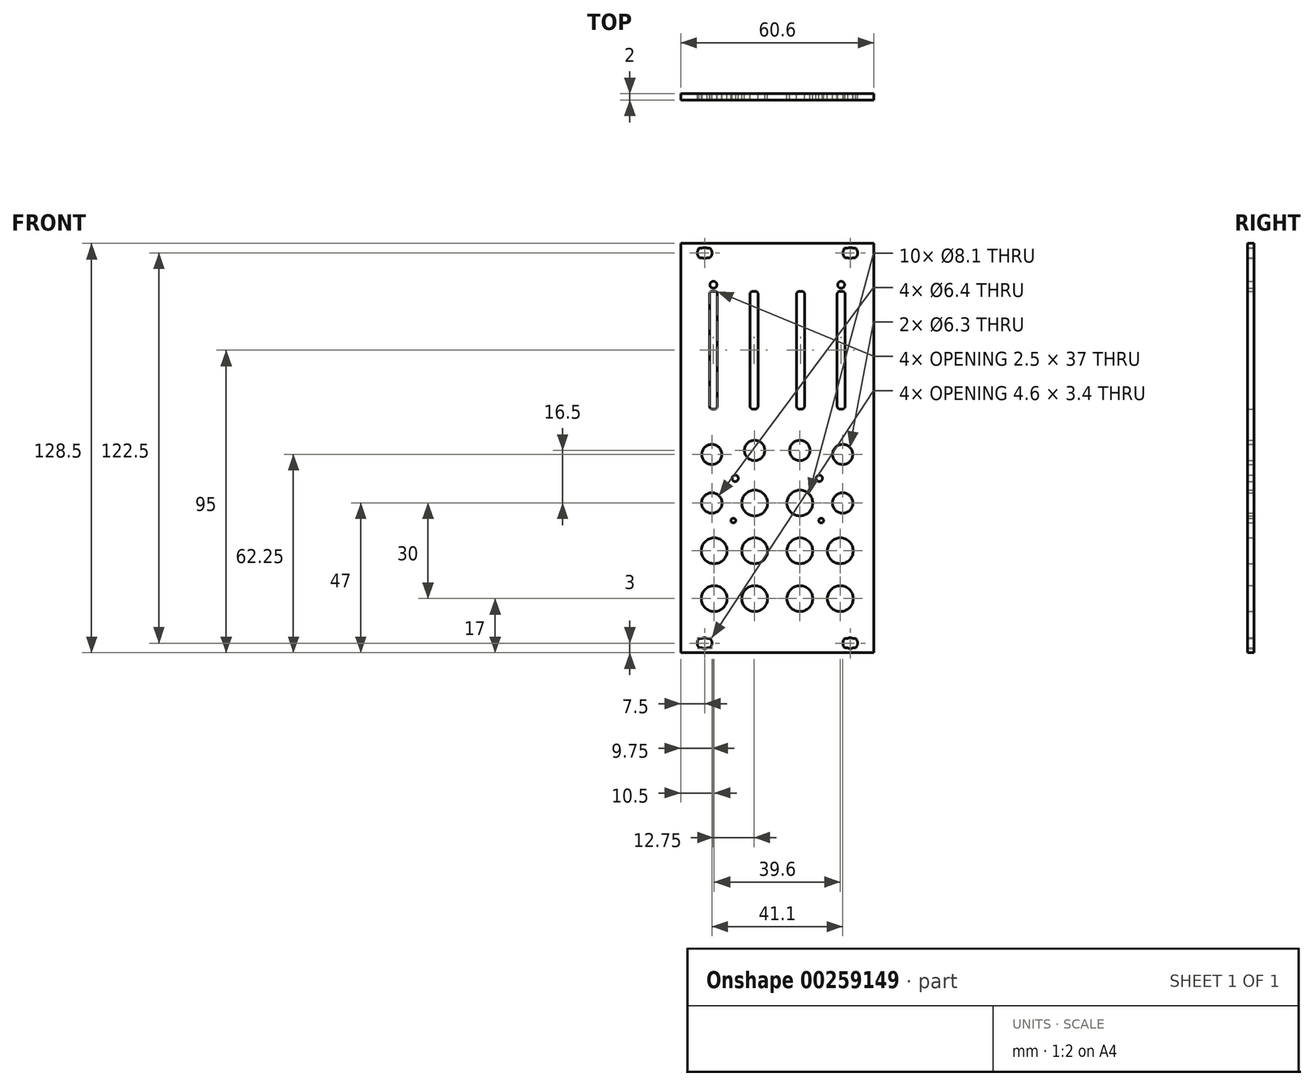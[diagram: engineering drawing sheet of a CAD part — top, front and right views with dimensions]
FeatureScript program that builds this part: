
annotation { "Feature Type Name" : "Feature", "Feature Type Description" : "" }
export const myFeature = defineFeature(function(context is Context, id is Id, definition is map)
    precondition{}
    {
        {
            var Q0;
            Q0=qCreatedBy(makeId("Front.planeOp"),FACE);
            var sketch = newSketch(context, id + "F0", { "sketchPlane" : qUnion([Q0])});
            skLineSegment(sketch, "E0", {"start": v(23.72, -59.75) * mm, "end": v(24.62, -59.75) * mm});
            skLineSegment(sketch, "E1", {"start": v(21.22, -59.75) * mm, "end": v(22.12, -59.75) * mm});
            skLineSegment(sketch, "E2", {"start": v(23.72, -62.75) * mm, "end": v(24.62, -62.75) * mm});
            skLineSegment(sketch, "E3", {"start": v(21.22, -62.75) * mm, "end": v(22.12, -62.75) * mm});
            skLineSegment(sketch, "E4", {"start": v(21.22, 59.75) * mm, "end": v(22.12, 59.75) * mm});
            skLineSegment(sketch, "E5", {"start": v(23.72, 59.75) * mm, "end": v(24.62, 59.75) * mm});
            skLineSegment(sketch, "E6", {"start": v(21.22, 62.75) * mm, "end": v(22.12, 62.75) * mm});
            skLineSegment(sketch, "E7", {"start": v(23.72, 62.75) * mm, "end": v(24.62, 62.75) * mm});
            skLineSegment(sketch, "E8", {"start": v(-30.3, -64.25) * mm, "end": v(-30.3, -61.25) * mm});
            skLineSegment(sketch, "E9", {"start": v(-30.3, 64.25) * mm, "end": v(30.3, 64.25) * mm});
            skLineSegment(sketch, "E10", {"start": v(30.3, -64.25) * mm, "end": v(30.3, 64.25) * mm});
            skLineSegment(sketch, "E11", {"start": v(-30.3, -64.25) * mm, "end": v(30.3, -64.25) * mm});
            skLineSegment(sketch, "E12", {"start": v(-30.3, -64.25) * mm, "end": v(-30.3, 64.25) * mm});
            skLineSegment(sketch, "E13", {"start": v(-22, -59.75) * mm, "end": v(-21.1, -59.75) * mm});
            skLineSegment(sketch, "E14", {"start": v(-24.5, -59.75) * mm, "end": v(-23.6, -59.75) * mm});
            skLineSegment(sketch, "E15", {"start": v(-22, -62.75) * mm, "end": v(-21.1, -62.75) * mm});
            skLineSegment(sketch, "E16", {"start": v(-24.5, -62.75) * mm, "end": v(-23.6, -62.75) * mm});
            skLineSegment(sketch, "E17", {"start": v(-22, 62.75) * mm, "end": v(-21.1, 62.75) * mm});
            skLineSegment(sketch, "E18", {"start": v(-24.5, 62.75) * mm, "end": v(-23.6, 62.75) * mm});
            skLineSegment(sketch, "E19", {"start": v(-22, 59.75) * mm, "end": v(-21.1, 59.75) * mm});
            skLineSegment(sketch, "E20", {"start": v(-24.5, 59.75) * mm, "end": v(-23.6, 59.75) * mm});
            skArc(sketch, "E21", {"start": v(21.22, -59.75) * mm, "mid": v(20.62, -61.25) * mm, "end": v(21.22, -62.75) * mm});
            skArc(sketch, "E22", {"start": v(24.62, -62.75) * mm, "mid": v(25.22, -61.25) * mm, "end": v(24.62, -59.75) * mm});
            skArc(sketch, "E23", {"start": v(23.72, -59.75) * mm, "mid": v(22.92, -59.55) * mm, "end": v(22.12, -59.75) * mm});
            skArc(sketch, "E24", {"start": v(22.12, -62.75) * mm, "mid": v(22.92, -62.95) * mm, "end": v(23.72, -62.75) * mm});
            skArc(sketch, "E25", {"start": v(22.12, 59.75) * mm, "mid": v(22.92, 59.55) * mm, "end": v(23.72, 59.75) * mm});
            skArc(sketch, "E26", {"start": v(23.72, 62.75) * mm, "mid": v(22.92, 62.95) * mm, "end": v(22.12, 62.75) * mm});
            skArc(sketch, "E27", {"start": v(24.62, 59.75) * mm, "mid": v(25.22, 61.25) * mm, "end": v(24.62, 62.75) * mm});
            skArc(sketch, "E28", {"start": v(21.22, 62.75) * mm, "mid": v(20.62, 61.25) * mm, "end": v(21.22, 59.75) * mm});
            skArc(sketch, "E29", {"start": v(-24.5, -59.75) * mm, "mid": v(-25.1, -61.25) * mm, "end": v(-24.5, -62.75) * mm});
            skArc(sketch, "E30", {"start": v(-21.1, -62.75) * mm, "mid": v(-20.5, -61.25) * mm, "end": v(-21.1, -59.75) * mm});
            skArc(sketch, "E31", {"start": v(-22, -59.75) * mm, "mid": v(-22.8, -59.55) * mm, "end": v(-23.6, -59.75) * mm});
            skArc(sketch, "E32", {"start": v(-23.6, -62.75) * mm, "mid": v(-22.8, -62.95) * mm, "end": v(-22, -62.75) * mm});
            skArc(sketch, "E33", {"start": v(-24.5, 62.75) * mm, "mid": v(-25.1, 61.25) * mm, "end": v(-24.5, 59.75) * mm});
            skArc(sketch, "E34", {"start": v(-21.1, 59.75) * mm, "mid": v(-20.5, 61.25) * mm, "end": v(-21.1, 62.75) * mm});
            skArc(sketch, "E35", {"start": v(-22, 62.75) * mm, "mid": v(-22.8, 62.95) * mm, "end": v(-23.6, 62.75) * mm});
            skArc(sketch, "E36", {"start": v(-23.6, 59.75) * mm, "mid": v(-22.8, 59.55) * mm, "end": v(-22, 59.75) * mm});
            skLineSegment(sketch, "E37", {"start": v(13.3, -22.75) * mm, "end": v(14.3, -22.75) * mm});
            skLineSegment(sketch, "E38", {"start": v(13.8, -23.25) * mm, "end": v(13.8, -22.25) * mm});
            skLineSegment(sketch, "E39", {"start": v(-20.55, -2.5) * mm, "end": v(-20.55, -1.5) * mm});
            skLineSegment(sketch, "E40", {"start": v(-21.05, -2) * mm, "end": v(-20.05, -2) * mm});
            skCircle(sketch, "E41", {"center": v(-20.55, -2) * mm, "radius": 3.15 * mm});
            skLineSegment(sketch, "E42", {"start": v(20.55, -2.5) * mm, "end": v(20.55, -1.5) * mm});
            skLineSegment(sketch, "E43", {"start": v(20.05, -2) * mm, "end": v(21.05, -2) * mm});
            skCircle(sketch, "E44", {"center": v(20.55, -2) * mm, "radius": 3.15 * mm});
            skLineSegment(sketch, "E45", {"start": v(6.05, 30.75) * mm, "end": v(6.05, 48.35) * mm});
            skLineSegment(sketch, "E46", {"start": v(6.05, 13.15) * mm, "end": v(6.05, 30.75) * mm});
            skLineSegment(sketch, "E47", {"start": v(6.95, 12.25) * mm, "end": v(7.65, 12.25) * mm});
            skLineSegment(sketch, "E48", {"start": v(7.3, 30.25) * mm, "end": v(7.3, 31.25) * mm});
            skLineSegment(sketch, "E49", {"start": v(8.55, 13.15) * mm, "end": v(8.55, 30.75) * mm});
            skLineSegment(sketch, "E50", {"start": v(6.8, 30.75) * mm, "end": v(7.8, 30.75) * mm});
            skLineSegment(sketch, "E51", {"start": v(6.95, 49.25) * mm, "end": v(7.65, 49.25) * mm});
            skLineSegment(sketch, "E52", {"start": v(8.55, 30.75) * mm, "end": v(8.55, 48.35) * mm});
            skArc(sketch, "E53", {"start": v(6.05, 13.15) * mm, "mid": v(6.31, 12.51) * mm, "end": v(6.95, 12.25) * mm});
            skArc(sketch, "E54", {"start": v(6.95, 49.25) * mm, "mid": v(6.31, 48.99) * mm, "end": v(6.05, 48.35) * mm});
            skArc(sketch, "E55", {"start": v(7.65, 12.25) * mm, "mid": v(8.29, 12.51) * mm, "end": v(8.55, 13.15) * mm});
            skArc(sketch, "E56", {"start": v(8.55, 48.35) * mm, "mid": v(8.29, 48.99) * mm, "end": v(7.65, 49.25) * mm});
            skLineSegment(sketch, "E57", {"start": v(-8.55, 30.75) * mm, "end": v(-8.55, 48.35) * mm});
            skLineSegment(sketch, "E58", {"start": v(-8.55, 13.15) * mm, "end": v(-8.55, 30.75) * mm});
            skLineSegment(sketch, "E59", {"start": v(-7.65, 12.25) * mm, "end": v(-6.95, 12.25) * mm});
            skLineSegment(sketch, "E60", {"start": v(-7.3, 30.25) * mm, "end": v(-7.3, 31.25) * mm});
            skLineSegment(sketch, "E61", {"start": v(-6.05, 13.15) * mm, "end": v(-6.05, 30.75) * mm});
            skLineSegment(sketch, "E62", {"start": v(-7.8, 30.75) * mm, "end": v(-6.8, 30.75) * mm});
            skLineSegment(sketch, "E63", {"start": v(-7.65, 49.25) * mm, "end": v(-6.95, 49.25) * mm});
            skLineSegment(sketch, "E64", {"start": v(-6.05, 30.75) * mm, "end": v(-6.05, 48.35) * mm});
            skArc(sketch, "E65", {"start": v(-8.55, 13.15) * mm, "mid": v(-8.29, 12.51) * mm, "end": v(-7.65, 12.25) * mm});
            skArc(sketch, "E66", {"start": v(-7.65, 49.25) * mm, "mid": v(-8.29, 48.99) * mm, "end": v(-8.55, 48.35) * mm});
            skArc(sketch, "E67", {"start": v(-6.95, 12.25) * mm, "mid": v(-6.31, 12.51) * mm, "end": v(-6.05, 13.15) * mm});
            skArc(sketch, "E68", {"start": v(-6.05, 48.35) * mm, "mid": v(-6.31, 48.99) * mm, "end": v(-6.95, 49.25) * mm});
            skLineSegment(sketch, "E69", {"start": v(18.8, 30.75) * mm, "end": v(18.8, 48.35) * mm});
            skLineSegment(sketch, "E70", {"start": v(18.8, 13.15) * mm, "end": v(18.8, 30.75) * mm});
            skLineSegment(sketch, "E71", {"start": v(19.7, 12.25) * mm, "end": v(20.4, 12.25) * mm});
            skLineSegment(sketch, "E72", {"start": v(20.05, 30.25) * mm, "end": v(20.05, 31.25) * mm});
            skLineSegment(sketch, "E73", {"start": v(21.3, 13.15) * mm, "end": v(21.3, 30.75) * mm});
            skLineSegment(sketch, "E74", {"start": v(19.55, 30.75) * mm, "end": v(20.55, 30.75) * mm});
            skLineSegment(sketch, "E75", {"start": v(19.7, 49.25) * mm, "end": v(20.4, 49.25) * mm});
            skLineSegment(sketch, "E76", {"start": v(21.3, 30.75) * mm, "end": v(21.3, 48.35) * mm});
            skArc(sketch, "E77", {"start": v(18.8, 13.15) * mm, "mid": v(19.06, 12.51) * mm, "end": v(19.7, 12.25) * mm});
            skArc(sketch, "E78", {"start": v(19.7, 49.25) * mm, "mid": v(19.06, 48.99) * mm, "end": v(18.8, 48.35) * mm});
            skArc(sketch, "E79", {"start": v(20.4, 12.25) * mm, "mid": v(21.04, 12.51) * mm, "end": v(21.3, 13.15) * mm});
            skArc(sketch, "E80", {"start": v(21.3, 48.35) * mm, "mid": v(21.04, 48.99) * mm, "end": v(20.4, 49.25) * mm});
            skLineSegment(sketch, "E81", {"start": v(-21.3, 30.75) * mm, "end": v(-21.3, 48.35) * mm});
            skLineSegment(sketch, "E82", {"start": v(-21.3, 13.15) * mm, "end": v(-21.3, 30.75) * mm});
            skLineSegment(sketch, "E83", {"start": v(-20.4, 12.25) * mm, "end": v(-19.7, 12.25) * mm});
            skLineSegment(sketch, "E84", {"start": v(-20.05, 30.25) * mm, "end": v(-20.05, 31.25) * mm});
            skLineSegment(sketch, "E85", {"start": v(-18.8, 13.15) * mm, "end": v(-18.8, 30.75) * mm});
            skLineSegment(sketch, "E86", {"start": v(-20.55, 30.75) * mm, "end": v(-19.55, 30.75) * mm});
            skLineSegment(sketch, "E87", {"start": v(-20.4, 49.25) * mm, "end": v(-19.7, 49.25) * mm});
            skLineSegment(sketch, "E88", {"start": v(-18.8, 30.75) * mm, "end": v(-18.8, 48.35) * mm});
            skArc(sketch, "E89", {"start": v(-21.3, 13.15) * mm, "mid": v(-21.04, 12.51) * mm, "end": v(-20.4, 12.25) * mm});
            skArc(sketch, "E90", {"start": v(-20.4, 49.25) * mm, "mid": v(-21.04, 48.99) * mm, "end": v(-21.3, 48.35) * mm});
            skArc(sketch, "E91", {"start": v(-19.7, 12.25) * mm, "mid": v(-19.06, 12.51) * mm, "end": v(-18.8, 13.15) * mm});
            skArc(sketch, "E92", {"start": v(-18.8, 48.35) * mm, "mid": v(-19.06, 48.99) * mm, "end": v(-19.7, 49.25) * mm});
            skCircle(sketch, "E93", {"center": v(-20.05, 51.25) * mm, "radius": 1.1 * mm});
            skLineSegment(sketch, "E94", {"start": v(-14.3, -22.75) * mm, "end": v(-13.3, -22.75) * mm});
            skLineSegment(sketch, "E95", {"start": v(-13.8, -23.25) * mm, "end": v(-13.8, -22.25) * mm});
            skLineSegment(sketch, "E96", {"start": v(13.2, -10) * mm, "end": v(13.2, -9) * mm});
            skLineSegment(sketch, "E97", {"start": v(12.7, -9.5) * mm, "end": v(13.7, -9.5) * mm});
            skLineSegment(sketch, "E98", {"start": v(-13.2, -10) * mm, "end": v(-13.2, -9) * mm});
            skLineSegment(sketch, "E99", {"start": v(-13.7, -9.5) * mm, "end": v(-12.7, -9.5) * mm});
            skLineSegment(sketch, "E100", {"start": v(7.1, -1.25) * mm, "end": v(7.1, -0.25) * mm});
            skLineSegment(sketch, "E101", {"start": v(6.6, -0.75) * mm, "end": v(7.6, -0.75) * mm});
            skCircle(sketch, "E102", {"center": v(7.1, -0.75) * mm, "radius": 3.2 * mm});
            skLineSegment(sketch, "E103", {"start": v(-7.1, -1.25) * mm, "end": v(-7.1, -0.25) * mm});
            skLineSegment(sketch, "E104", {"start": v(-7.6, -0.75) * mm, "end": v(-6.6, -0.75) * mm});
            skCircle(sketch, "E105", {"center": v(-7.1, -0.75) * mm, "radius": 3.2 * mm});
            skLineSegment(sketch, "E106", {"start": v(20.55, -17.75) * mm, "end": v(20.55, -16.75) * mm});
            skLineSegment(sketch, "E107", {"start": v(20.05, -17.25) * mm, "end": v(21.05, -17.25) * mm});
            skCircle(sketch, "E108", {"center": v(20.55, -17.25) * mm, "radius": 3.2 * mm});
            skLineSegment(sketch, "E109", {"start": v(-20.55, -17.75) * mm, "end": v(-20.55, -16.75) * mm});
            skLineSegment(sketch, "E110", {"start": v(-21.05, -17.25) * mm, "end": v(-20.05, -17.25) * mm});
            skCircle(sketch, "E111", {"center": v(-20.55, -17.25) * mm, "radius": 3.2 * mm});
            skLineSegment(sketch, "E112", {"start": v(6.35, -17.25) * mm, "end": v(7.85, -17.25) * mm});
            skLineSegment(sketch, "E113", {"start": v(7.1, -18) * mm, "end": v(7.1, -16.5) * mm});
            skCircle(sketch, "E114", {"center": v(7.1, -17.25) * mm, "radius": 4.05 * mm});
            skLineSegment(sketch, "E115", {"start": v(19.05, -32.25) * mm, "end": v(20.55, -32.25) * mm});
            skLineSegment(sketch, "E116", {"start": v(19.8, -33) * mm, "end": v(19.8, -31.5) * mm});
            skCircle(sketch, "E117", {"center": v(19.8, -32.25) * mm, "radius": 4.05 * mm});
            skLineSegment(sketch, "E118", {"start": v(6.35, -32.25) * mm, "end": v(7.85, -32.25) * mm});
            skLineSegment(sketch, "E119", {"start": v(7.1, -33) * mm, "end": v(7.1, -31.5) * mm});
            skCircle(sketch, "E120", {"center": v(7.1, -32.25) * mm, "radius": 4.05 * mm});
            skLineSegment(sketch, "E121", {"start": v(19.05, -47.25) * mm, "end": v(20.55, -47.25) * mm});
            skLineSegment(sketch, "E122", {"start": v(19.8, -48) * mm, "end": v(19.8, -46.5) * mm});
            skCircle(sketch, "E123", {"center": v(19.8, -47.25) * mm, "radius": 4.05 * mm});
            skLineSegment(sketch, "E124", {"start": v(6.35, -47.25) * mm, "end": v(7.85, -47.25) * mm});
            skLineSegment(sketch, "E125", {"start": v(7.1, -48) * mm, "end": v(7.1, -46.5) * mm});
            skCircle(sketch, "E126", {"center": v(7.1, -47.25) * mm, "radius": 4.05 * mm});
            skLineSegment(sketch, "E127", {"start": v(-7.85, -17.25) * mm, "end": v(-6.35, -17.25) * mm});
            skLineSegment(sketch, "E128", {"start": v(-7.1, -18) * mm, "end": v(-7.1, -16.5) * mm});
            skCircle(sketch, "E129", {"center": v(-7.1, -17.25) * mm, "radius": 4.05 * mm});
            skLineSegment(sketch, "E130", {"start": v(-20.55, -32.25) * mm, "end": v(-19.05, -32.25) * mm});
            skLineSegment(sketch, "E131", {"start": v(-19.8, -33) * mm, "end": v(-19.8, -31.5) * mm});
            skCircle(sketch, "E132", {"center": v(-19.8, -32.25) * mm, "radius": 4.05 * mm});
            skLineSegment(sketch, "E133", {"start": v(-7.85, -32.25) * mm, "end": v(-6.35, -32.25) * mm});
            skLineSegment(sketch, "E134", {"start": v(-7.1, -33) * mm, "end": v(-7.1, -31.5) * mm});
            skCircle(sketch, "E135", {"center": v(-7.1, -32.25) * mm, "radius": 4.05 * mm});
            skLineSegment(sketch, "E136", {"start": v(-20.55, -47.25) * mm, "end": v(-19.05, -47.25) * mm});
            skLineSegment(sketch, "E137", {"start": v(-19.8, -48) * mm, "end": v(-19.8, -46.5) * mm});
            skCircle(sketch, "E138", {"center": v(-19.8, -47.25) * mm, "radius": 4.05 * mm});
            skLineSegment(sketch, "E139", {"start": v(-7.85, -47.25) * mm, "end": v(-6.35, -47.25) * mm});
            skLineSegment(sketch, "E140", {"start": v(-7.1, -48) * mm, "end": v(-7.1, -46.5) * mm});
            skCircle(sketch, "E141", {"center": v(-7.1, -47.25) * mm, "radius": 4.05 * mm});
            skLineSegment(sketch, "E142", {"start": v(19.42, 51.25) * mm, "end": v(20.69, 51.25) * mm});
            skLineSegment(sketch, "E143", {"start": v(20.05, 50.62) * mm, "end": v(20.05, 51.89) * mm});
            skCircle(sketch, "E144", {"center": v(20.05, 51.25) * mm, "radius": 1.1 * mm});
            skLineSegment(sketch, "E145", {"start": v(-20.69, 51.25) * mm, "end": v(-19.41, 51.25) * mm});
            skLineSegment(sketch, "E146", {"start": v(-20.05, 50.62) * mm, "end": v(-20.05, 51.89) * mm});
            skCircle(sketch, "E147", {"center": v(-13.8, -22.75) * mm, "radius": 0.75 * mm});
            skCircle(sketch, "E148", {"center": v(-13.2, -9.5) * mm, "radius": 1 * mm});
            skCircle(sketch, "E149", {"center": v(13.2, -9.5) * mm, "radius": 1 * mm});
            skCircle(sketch, "E150", {"center": v(13.8, -22.75) * mm, "radius": 0.75 * mm});
            skSolve(sketch);
        }
        {
            var Q0;
            Q0 = qSketchRegion(id + "F0", true);
            extrude(context, id + "F1", {"entities" : qUnion([Q0]), "depth" : 2 * mm});
        }
    });
